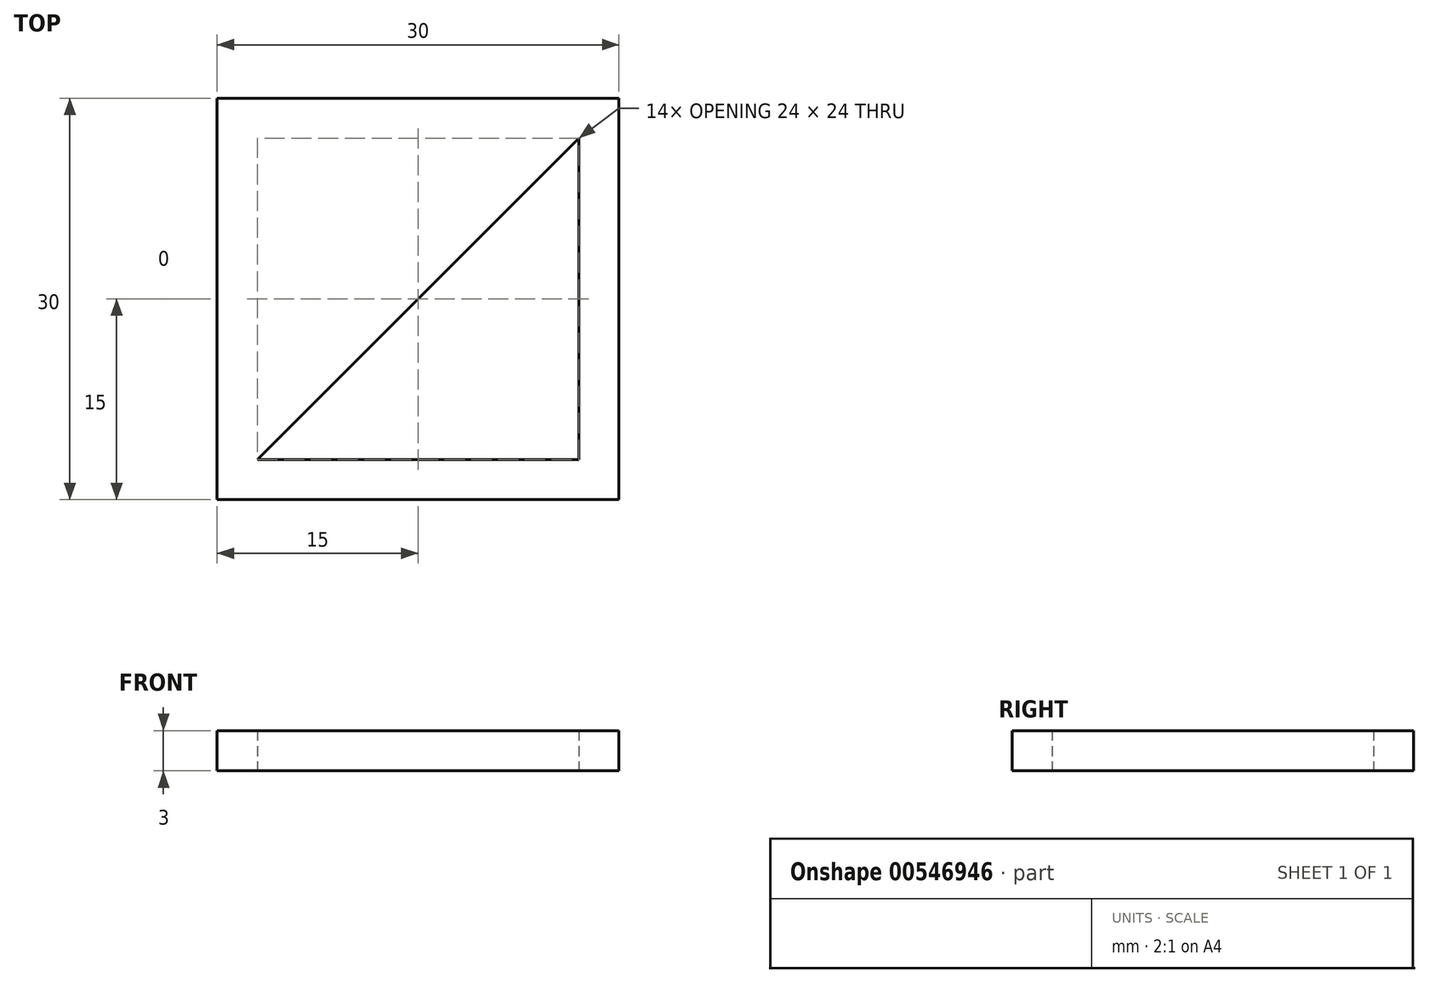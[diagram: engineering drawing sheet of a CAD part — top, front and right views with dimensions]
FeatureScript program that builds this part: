
annotation { "Feature Type Name" : "Feature", "Feature Type Description" : "" }
export const myFeature = defineFeature(function(context is Context, id is Id, definition is map)
    precondition{}
    {
        {
            var Q0;
            Q0=qCreatedBy(makeId("Top.planeOp"),FACE);
            var sketch = newSketch(context, id + "F0", { "sketchPlane" : qUnion([Q0])});
            skLineSegment(sketch, "E0.bottom", {"start": v(-15, 15) * mm, "end": v(15, 15) * mm});
            skLineSegment(sketch, "E0.top", {"start": v(-15, -15) * mm, "end": v(15, -15) * mm});
            skLineSegment(sketch, "E0.left", {"start": v(-15, 15) * mm, "end": v(-15, -15) * mm});
            skLineSegment(sketch, "E0.right", {"start": v(15, 15) * mm, "end": v(15, -15) * mm});
            skPoint(sketch, "E0.middle", {"position": v(0, 0) * mm});
            skLineSegment(sketch, "E1.2", {"start": v(12, 12) * mm, "end": v(12, -12) * mm});
            skLineSegment(sketch, "E1.3", {"start": v(-12, -12) * mm, "end": v(12, -12) * mm});
            skLineSegment(sketch, "E2", {"start": v(-12, -12) * mm, "end": v(12, 12) * mm});
            skSolve(sketch);
        }
        {
            var Q0;
            Q0 = qSketchRegion(id + "F0", true);
            extrude(context, id + "F1", {"entities" : qUnion([Q0]), "depth" : 3 * mm, "offsetDistance" : 25 * mm});
        }
    });
